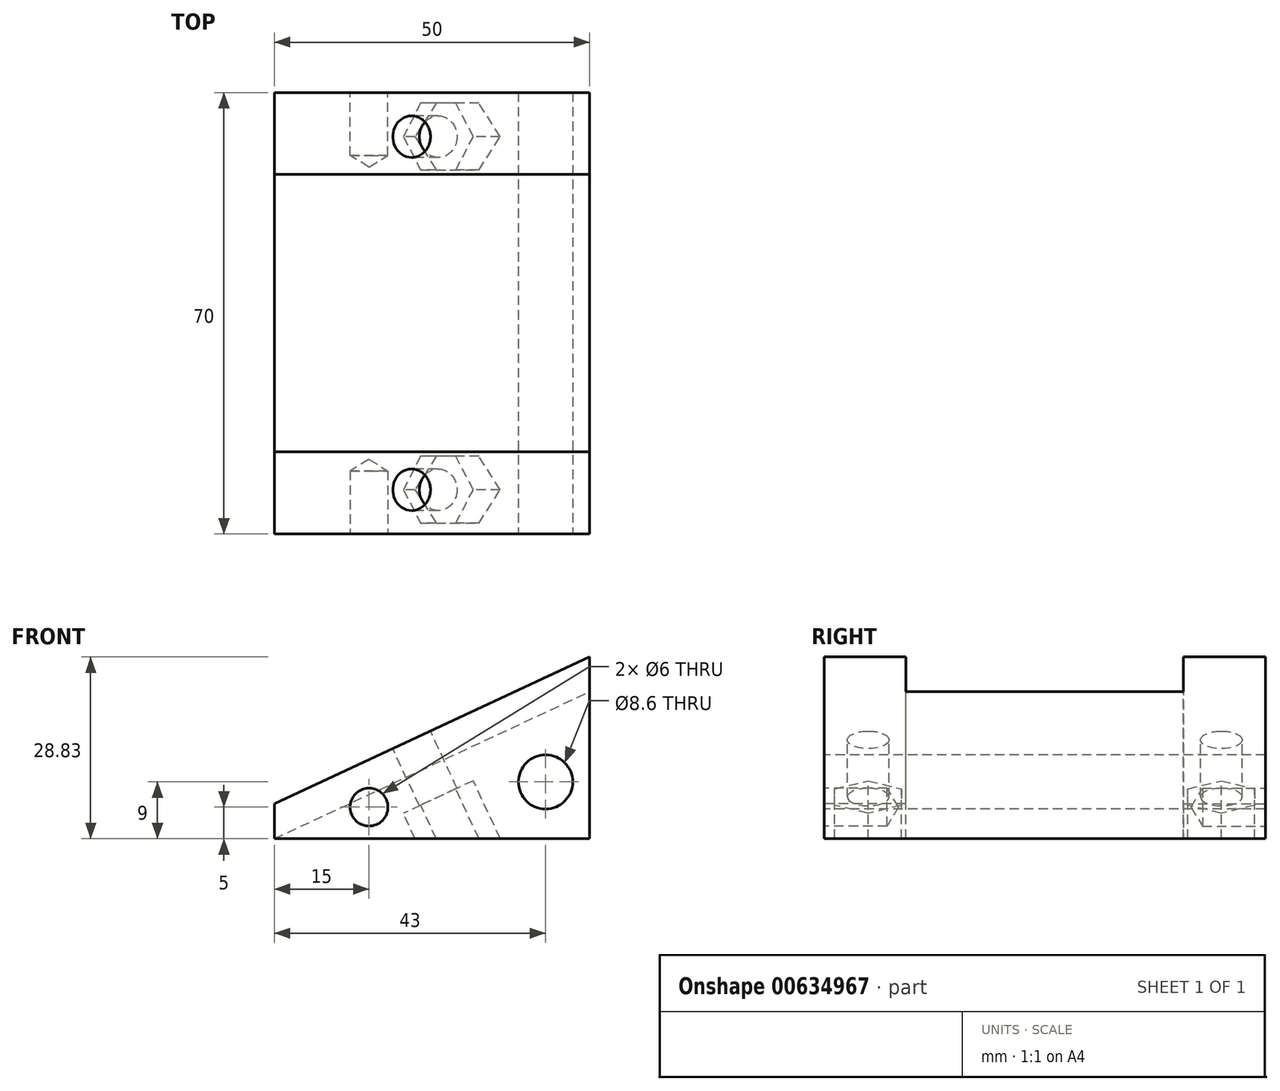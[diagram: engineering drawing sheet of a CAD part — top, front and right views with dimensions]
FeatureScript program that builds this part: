
annotation { "Feature Type Name" : "Feature", "Feature Type Description" : "" }
export const myFeature = defineFeature(function(context is Context, id is Id, definition is map)
    precondition{}
    {
        {
            var Q0;
            Q0=qCreatedBy(makeId("Front.planeOp"),FACE);
            var sketch = newSketch(context, id + "F0", { "sketchPlane" : qUnion([Q0])});
            skLineSegment(sketch, "E0", {"start": v(0, 0) * mm, "end": v(50, 0) * mm});
            skLineSegment(sketch, "E1", {"start": v(0, 0) * mm, "end": v(50, 23.32) * mm});
            skLineSegment(sketch, "E2", {"start": v(50, 0) * mm, "end": v(50, 23.32) * mm});
            skLineSegment(sketch, "E3", {"start": v(51.9, 27.35) * mm, "end": v(-4.86, 0.89) * mm, "construction": true});
            skSolve(sketch);
        }
        {
            var Q0;
            Q0=makeQuery(id+"F0.imprint","IMPRINT",FACE,{"disambiguationData":[TD([[makeQuery(id+"F0.imprint","IMPRINT",EDGE,{"derivedFrom":sQuery(id+"F0.wireOp",EDGE,"E0")}),1.0]])]});
            extrude(context, id + "F1", {"entities" : qUnion([Q0]), "endBound" : BoundingType.SYMMETRIC, "depth" : 70 * mm, "offsetDistance" : 25 * mm});
        }
        {
            var Q0;
            Q0=makeQuery(id+"F1.opExtrude","SWEPT_EDGE",EDGE,{"disambiguationData":[OSD([sQuery(id+"F0.wireOp",EDGE,"E0"),sQuery(id+"F0.wireOp",EDGE,"E1")])]});
            cPoint(context, id + "F2", {"entities" : qUnion([Q0]), "parameter" : 0.5});
        }
        {
            var Q0;
            Q0 = qCreatedBy(id + "F2" ,VERTEX);
            var Q1;
            Q1=makeQuery(id+"F1.opExtrude","CAP_VERTEX",VERTEX,{"disambiguationData":[OSD([sQuery(id+"F0.wireOp",EDGE,"E1"),sQuery(id+"F0.wireOp",EDGE,"E2")])],"isStart":false});
            var Q2;
            Q2=makeQuery(id+"F1.opExtrude","CAP_VERTEX",VERTEX,{"disambiguationData":[OSD([sQuery(id+"F0.wireOp",EDGE,"E1"),sQuery(id+"F0.wireOp",EDGE,"E2")])],"isStart":true});
            cPlane(context, id + "F3", {"entities" : qUnion([Q0, Q1, Q2]), "cplaneType" : CPlaneType.THREE_POINT, "offset" : 25 * mm, "width" : 150 * mm, "height" : 150 * mm});
        }
        {
            var Q0;
            Q0=makeQuery(id+"F1.opExtrude","CAP_FACE",FACE,{"disambiguationData":[OSD([sQuery(id+"F0.wireOp",EDGE,"E0"),sQuery(id+"F0.wireOp",EDGE,"E1"),sQuery(id+"F0.wireOp",EDGE,"E2")])],"isStart":false});
            var sketch = newSketch(context, id + "F4", { "sketchPlane" : qUnion([Q0])});
            skLineSegment(sketch, "E4.0", {"start": v(-2.11, 4.53) * mm, "end": v(47.89, 27.85) * mm, "construction": true});
            skLineSegment(sketch, "E5", {"start": v(0, 0) * mm, "end": v(0, 5.52) * mm});
            skLineSegment(sketch, "E6", {"start": v(0, 5.52) * mm, "end": v(50, 28.83) * mm});
            skLineSegment(sketch, "E7", {"start": v(50, 28.83) * mm, "end": v(50, 23.32) * mm});
            skSolve(sketch);
        }
        {
            var Q0;
            Q0=makeQuery(id+"F4.imprint","IMPRINT",FACE,{"disambiguationData":[TD([[makeQuery(id+"F4.imprint","IMPRINT",EDGE,{"derivedFrom":sQuery(id+"F4.wireOp",EDGE,"E5")}),-1.0]])]});
            extrude(context, id + "F5", {"entities" : qUnion([Q0]), "operationType" : NewBodyOperationType.ADD, "oppositeDirection" : true, "depth" : 13 * mm, "offsetDistance" : 25 * mm});
        }
        {
            var Q0;
            Q0=makeQuery(id+"F1.opExtrude","CAP_FACE",FACE,{"disambiguationData":[OSD([sQuery(id+"F0.wireOp",EDGE,"E0"),sQuery(id+"F0.wireOp",EDGE,"E1"),sQuery(id+"F0.wireOp",EDGE,"E2")])],"isStart":true});
            var sketch = newSketch(context, id + "F6", { "sketchPlane" : qUnion([Q0])});
            skLineSegment(sketch, "E8", {"start": v(-50, 23.32) * mm, "end": v(-50, 28.83) * mm});
            skLineSegment(sketch, "E9", {"start": v(-50, 28.83) * mm, "end": v(0, 5.52) * mm});
            skLineSegment(sketch, "E10", {"start": v(0, 5.52) * mm, "end": v(0, 0) * mm});
            skLineSegment(sketch, "E11", {"start": v(0, 0) * mm, "end": v(-50, 23.32) * mm});
            skSolve(sketch);
        }
        {
            var Q0;
            Q0=makeQuery(id+"F6.imprint","IMPRINT",FACE,{"disambiguationData":[TD([[makeQuery(id+"F6.imprint","IMPRINT",EDGE,{"derivedFrom":sQuery(id+"F6.wireOp",EDGE,"E8")}),-1.0]])]});
            extrude(context, id + "F7", {"entities" : qUnion([Q0]), "operationType" : NewBodyOperationType.ADD, "oppositeDirection" : true, "depth" : 13 * mm, "offsetDistance" : 25 * mm});
        }
        {
            var Q0;
            Q0=makeQuery(id+"F7.opExtrude","SWEPT_FACE",FACE,{"disambiguationData":[OSD([sQuery(id+"F6.wireOp",EDGE,"E9")])]});
            var sketch = newSketch(context, id + "F8", { "sketchPlane" : qUnion([Q0])});
            skLineSegment(sketch, "E12", {"start": v(26.33, 44.58) * mm, "end": v(26.33, -44.62) * mm, "construction": true});
            skPoint(sketch, "E13", {"position": v(26.33, 28) * mm});
            skPoint(sketch, "E14", {"position": v(26.33, -28) * mm});
            skSolve(sketch);
        }
        {
            var Q0;
            Q0=sQuery(id+"F8.wireOp",VERTEX,"E13");
            var Q1;
            Q1=sQuery(id+"F8.wireOp",VERTEX,"E14");
            var Q2;
            Q2=makeQuery(id+"F1.opExtrude","SWEPT_BODY",BODY,{"disambiguationData":[OSD([sQuery(id+"F0.wireOp",EDGE,"E0"),sQuery(id+"F0.wireOp",EDGE,"E1"),sQuery(id+"F0.wireOp",EDGE,"E2")])]});
            hole(context, id + "F9", {"style" : HoleStyle.SIMPLE, "endStyle" : HoleEndStyle.THROUGH, "holeDiameter" : 6.6 * mm, "majorDiameter" : 5 * mm, "isTappedThrough" : true, "tappedDepth" : 12 * mm, "tapClearance" : 3, "locations" : qUnion([Q0, Q1]), "scope" : qUnion([Q2])});
        }
        {
            var Q0;
            Q0=qCreatedBy(id+"F3.planeOp",FACE);
            cPlane(context, id + "F10", {"entities" : qUnion([Q0]), "cplaneType" : CPlaneType.OFFSET, "offset" : 5 * mm, "width" : 150 * mm, "height" : 150 * mm});
        }
        {
            var Q0;
            Q0=qCreatedBy(id+"F10.planeOp",FACE);
            var sketch = newSketch(context, id + "F11", { "sketchPlane" : qUnion([Q0])});
            skPoint(sketch, "E15", {"position": v(26.33, -28) * mm});
            skCircle(sketch, "E16.cCircle", {"center": v(26.33, -28) * mm, "radius": 5.3 * mm, "construction": true});
            skLineSegment(sketch, "E16.0", {"start": v(23.27, -33.3) * mm, "end": v(20.21, -28) * mm});
            skLineSegment(sketch, "E16.1", {"start": v(20.21, -28) * mm, "end": v(23.27, -22.7) * mm});
            skLineSegment(sketch, "E16.2", {"start": v(23.27, -22.7) * mm, "end": v(29.4, -22.7) * mm});
            skLineSegment(sketch, "E16.3", {"start": v(29.4, -22.7) * mm, "end": v(32.45, -28) * mm});
            skLineSegment(sketch, "E16.4", {"start": v(32.45, -28) * mm, "end": v(29.4, -33.3) * mm});
            skLineSegment(sketch, "E16.5", {"start": v(29.4, -33.3) * mm, "end": v(23.27, -33.3) * mm});
            skPoint(sketch, "E16.0.midPoint", {"position": v(21.74, -30.65) * mm});
            skPoint(sketch, "E17", {"position": v(26.33, 28) * mm});
            skCircle(sketch, "E18.cCircle", {"center": v(26.33, 28) * mm, "radius": 5.3 * mm, "construction": true});
            skLineSegment(sketch, "E18.0", {"start": v(23.27, 22.7) * mm, "end": v(20.21, 28) * mm});
            skLineSegment(sketch, "E18.1", {"start": v(20.21, 28) * mm, "end": v(23.27, 33.3) * mm});
            skLineSegment(sketch, "E18.2", {"start": v(23.27, 33.3) * mm, "end": v(29.4, 33.3) * mm});
            skLineSegment(sketch, "E18.3", {"start": v(29.4, 33.3) * mm, "end": v(32.45, 28) * mm});
            skLineSegment(sketch, "E18.4", {"start": v(32.45, 28) * mm, "end": v(29.4, 22.7) * mm});
            skLineSegment(sketch, "E18.5", {"start": v(29.4, 22.7) * mm, "end": v(23.27, 22.7) * mm});
            skPoint(sketch, "E18.0.midPoint", {"position": v(21.74, 25.35) * mm});
            skSolve(sketch);
        }
        {
            var Q0;
            Q0=makeQuery(id+"F11.imprint","IMPRINT",FACE,{"disambiguationData":[TD([[makeQuery(id+"F11.imprint","IMPRINT",EDGE,{"derivedFrom":sQuery(id+"F11.wireOp",EDGE,"E16.0")}),-1.0]])]});
            var Q1;
            Q1=makeQuery(id+"F11.imprint","IMPRINT",FACE,{"disambiguationData":[TD([[makeQuery(id+"F11.imprint","IMPRINT",EDGE,{"derivedFrom":sQuery(id+"F11.wireOp",EDGE,"E18.0")}),-1.0]])]});
            extrude(context, id + "F12", {"entities" : qUnion([Q0, Q1]), "operationType" : NewBodyOperationType.REMOVE, "depth" : 15 * mm, "offsetDistance" : 25 * mm});
        }
        {
            var Q0;
            {var subQ0=sQuery(id+"F0.wireOp",EDGE,"E1");Q0=makeQuery(id+"F5.boolean.opBoolean","MERGE",FACE,{"derivedFrom":[makeQuery(id+"F1.opExtrude","CAP_FACE",FACE,{"disambiguationData":[OSD([sQuery(id+"F0.wireOp",EDGE,"E0"),subQ0,sQuery(id+"F0.wireOp",EDGE,"E2")])],"isStart":false}),makeQuery(id+"F5.opExtrude","CAP_FACE",FACE,{"disambiguationData":[OSD([subQ0,sQuery(id+"F4.wireOp",EDGE,"E5"),sQuery(id+"F4.wireOp",EDGE,"E6"),sQuery(id+"F4.wireOp",EDGE,"E7")])],"isStart":true})]});}
            var sketch = newSketch(context, id + "F13", { "sketchPlane" : qUnion([Q0])});
            skPoint(sketch, "E19", {"position": v(43, 9) * mm});
            skSolve(sketch);
        }
        {
            var Q0;
            Q0=sQuery(id+"F13.wireOp",VERTEX,"E19");
            var Q1;
            Q1=makeQuery(id+"F1.opExtrude","SWEPT_BODY",BODY,{"disambiguationData":[OSD([sQuery(id+"F0.wireOp",EDGE,"E0"),sQuery(id+"F0.wireOp",EDGE,"E1"),sQuery(id+"F0.wireOp",EDGE,"E2")])]});
            hole(context, id + "F14", {"style" : HoleStyle.SIMPLE, "endStyle" : HoleEndStyle.THROUGH, "holeDiameter" : 8.6 * mm, "majorDiameter" : 5 * mm, "isTappedThrough" : true, "tappedDepth" : 12 * mm, "tapClearance" : 3, "locations" : qUnion([Q0]), "scope" : qUnion([Q1])});
        }
        {
            var Q0;
            Q0=makeQuery(id+"F7.opExtrude","SWEPT_FACE",FACE,{"disambiguationData":[OSD([sQuery(id+"F6.wireOp",EDGE,"E9")])]});
            var sketch = newSketch(context, id + "F15", { "sketchPlane" : qUnion([Q0])});
            skSolve(sketch);
        }
        {
            var Q0;
            {var subQ0=sQuery(id+"F0.wireOp",EDGE,"E1");Q0=makeQuery(id+"F5.boolean.opBoolean","MERGE",FACE,{"derivedFrom":[makeQuery(id+"F1.opExtrude","CAP_FACE",FACE,{"disambiguationData":[OSD([sQuery(id+"F0.wireOp",EDGE,"E0"),subQ0,sQuery(id+"F0.wireOp",EDGE,"E2")])],"isStart":false}),makeQuery(id+"F5.opExtrude","CAP_FACE",FACE,{"disambiguationData":[OSD([subQ0,sQuery(id+"F4.wireOp",EDGE,"E5"),sQuery(id+"F4.wireOp",EDGE,"E6"),sQuery(id+"F4.wireOp",EDGE,"E7")])],"isStart":true})]});}
            var sketch = newSketch(context, id + "F16", { "sketchPlane" : qUnion([Q0])});
            skPoint(sketch, "E20", {"position": v(15, 5) * mm});
            skSolve(sketch);
        }
        {
            var Q0;
            Q0=sQuery(id+"F16.wireOp",VERTEX,"E20");
            var Q1;
            Q1=makeQuery(id+"F1.opExtrude","SWEPT_BODY",BODY,{"disambiguationData":[OSD([sQuery(id+"F0.wireOp",EDGE,"E0"),sQuery(id+"F0.wireOp",EDGE,"E1"),sQuery(id+"F0.wireOp",EDGE,"E2")])]});
            hole(context, id + "F17", {"style" : HoleStyle.SIMPLE, "endStyle" : HoleEndStyle.BLIND, "holeDiameter" : 6 * mm, "majorDiameter" : 5 * mm, "holeDepth" : 10 * mm, "isTappedThrough" : true, "tappedDepth" : 12 * mm, "tapClearance" : 3, "locations" : qUnion([Q0]), "scope" : qUnion([Q1])});
        }
        {
            var Q0;
            Q0=makeQuery(id+"F7.boolean.opBoolean","MERGE",FACE,{"derivedFrom":[makeQuery(id+"F1.opExtrude","CAP_FACE",FACE,{"disambiguationData":[OSD([sQuery(id+"F0.wireOp",EDGE,"E0"),sQuery(id+"F0.wireOp",EDGE,"E1"),sQuery(id+"F0.wireOp",EDGE,"E2")])],"isStart":true}),makeQuery(id+"F7.opExtrude","CAP_FACE",FACE,{"disambiguationData":[OSD([sQuery(id+"F6.wireOp",EDGE,"E8"),sQuery(id+"F6.wireOp",EDGE,"E9"),sQuery(id+"F6.wireOp",EDGE,"E10"),sQuery(id+"F6.wireOp",EDGE,"E11")])],"isStart":true})]});
            var sketch = newSketch(context, id + "F18", { "sketchPlane" : qUnion([Q0])});
            skPoint(sketch, "E21", {"position": v(-15, 5) * mm});
            skSolve(sketch);
        }
        {
            var Q0;
            Q0=sQuery(id+"F18.wireOp",VERTEX,"E21");
            var Q1;
            Q1=makeQuery(id+"F1.opExtrude","SWEPT_BODY",BODY,{"disambiguationData":[OSD([sQuery(id+"F0.wireOp",EDGE,"E0"),sQuery(id+"F0.wireOp",EDGE,"E1"),sQuery(id+"F0.wireOp",EDGE,"E2")])]});
            hole(context, id + "F19", {"style" : HoleStyle.SIMPLE, "endStyle" : HoleEndStyle.BLIND, "holeDiameter" : 6 * mm, "majorDiameter" : 5 * mm, "holeDepth" : 10 * mm, "isTappedThrough" : true, "tappedDepth" : 12 * mm, "tapClearance" : 3, "locations" : qUnion([Q0]), "scope" : qUnion([Q1])});
        }
    });
